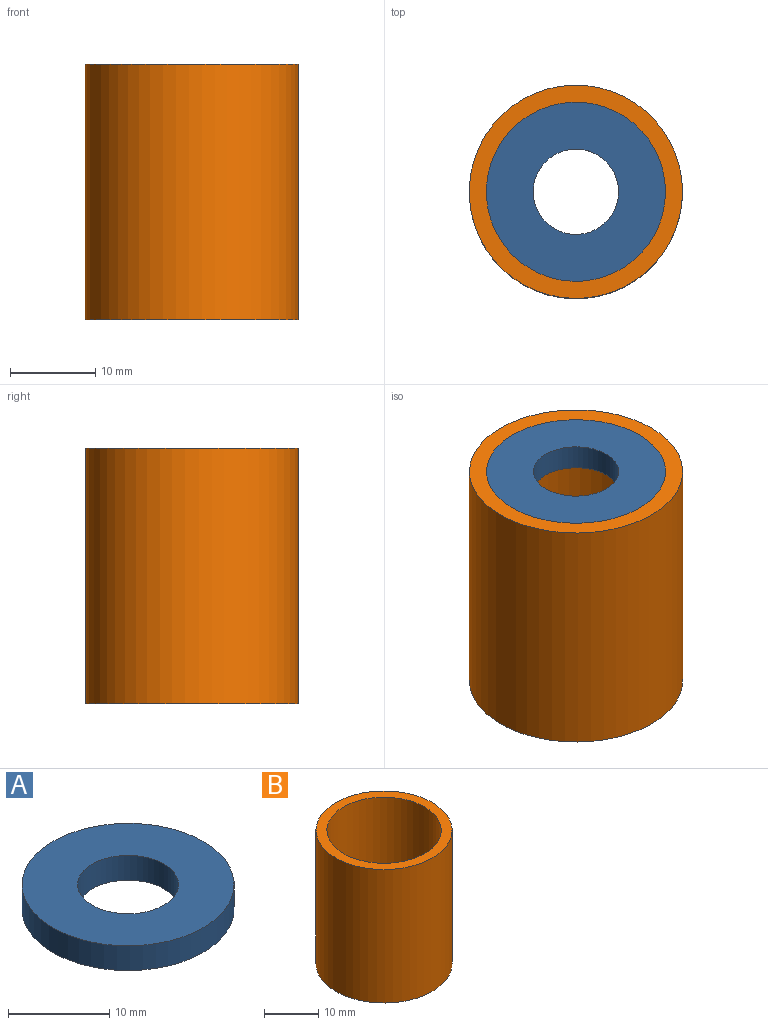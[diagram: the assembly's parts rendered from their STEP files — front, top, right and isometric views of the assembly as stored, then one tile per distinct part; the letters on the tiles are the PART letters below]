
ASSEMBLY  parts=2 mates=1
PART A: 4 faces, bbox 21x21x3 mm
  f0: cylinder r=5mm len=10mm, axis (0,0,-1), area 94.2mm2, adj f2,f3
  f1: cylinder r=10.5mm len=21mm, axis (0,0,-1), area 197.9mm2, adj f2,f3
  f2: plane 21x21mm, normal (0,0,1), area 267.8mm2, adj f0,f1
  f3: plane 21x21mm, normal (0,0,-1), area 267.8mm2, adj f0,f1
PART B: 4 faces, bbox 25x25x30 mm
  f0: cylinder r=10.5mm len=30mm, axis (0,0,-1), area 1979.2mm2, adj f2,f3
  f1: cylinder r=12.5mm len=30mm, axis (0,0,-1), area 2356.2mm2, adj f2,f3
  f2: plane 25x25mm, normal (0,0,1), area 144.5mm2, adj f0,f1
  f3: plane 25x25mm, normal (0,0,-1), area 144.5mm2, adj f0,f1
PLACE A t=(-0.08,-0.02,12.04)mm
PLACE B t=(-0.08,-0.02,-14.96)mm
MATE fastened A.f0 <-> B.f0  axis (0,0,1) through (-0.08,-0.02,15.04)mm
